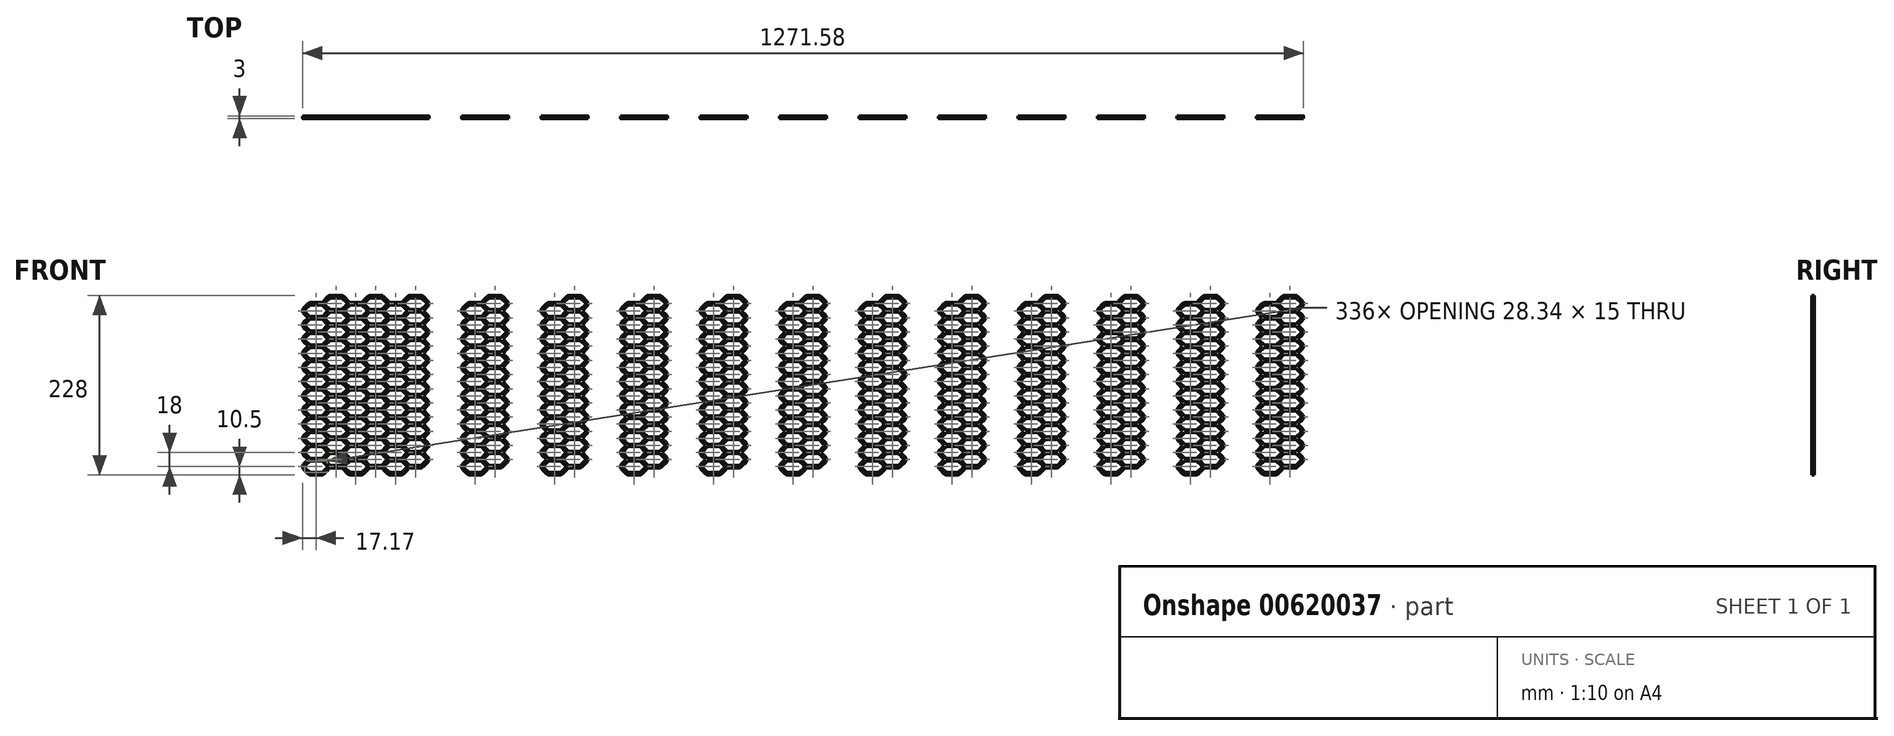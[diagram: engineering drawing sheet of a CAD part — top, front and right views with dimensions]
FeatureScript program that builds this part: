
annotation { "Feature Type Name" : "Feature", "Feature Type Description" : "" }
export const myFeature = defineFeature(function(context is Context, id is Id, definition is map)
    precondition{}
    {
        {
            var Q0;
            Q0=qCreatedBy(makeId("Front.planeOp"),FACE);
            var sketch = newSketch(context, id + "F0", { "sketchPlane" : qUnion([Q0])});
            skLineSegment(sketch, "E0.bottom", {"start": v(6.67, -7.5) * mm, "end": v(-6.67, -7.5) * mm});
            skLineSegment(sketch, "E0.top", {"start": v(6.67, 7.5) * mm, "end": v(-6.67, 7.5) * mm});
            skPoint(sketch, "E0.middle", {"position": v(0, 0) * mm});
            skLineSegment(sketch, "E1", {"start": v(-8.09, 6.91) * mm, "end": v(-13.59, 1.41) * mm});
            skLineSegment(sketch, "E2", {"start": v(-8.09, -6.91) * mm, "end": v(-13.59, -1.41) * mm});
            skLineSegment(sketch, "E3", {"start": v(8.09, 6.91) * mm, "end": v(13.59, 1.41) * mm});
            skLineSegment(sketch, "E4", {"start": v(13.59, -1.41) * mm, "end": v(8.09, -6.91) * mm});
            skPoint(sketch, "E5.visualSharp", {"position": v(-15, 0) * mm});
            skArc(sketch, "E5.filletArc", {"start": v(-13.59, 1.41) * mm, "mid": v(-14.17, 0) * mm, "end": v(-13.59, -1.41) * mm});
            skPoint(sketch, "E6.visualSharp", {"position": v(15, 0) * mm});
            skArc(sketch, "E6.filletArc", {"start": v(13.59, -1.41) * mm, "mid": v(14.17, 0) * mm, "end": v(13.59, 1.41) * mm});
            skPoint(sketch, "E7.visualSharp", {"position": v(7.5, -7.5) * mm});
            skArc(sketch, "E7.filletArc", {"start": v(6.67, -7.5) * mm, "mid": v(7.44, -7.35) * mm, "end": v(8.09, -6.91) * mm});
            skPoint(sketch, "E8.visualSharp", {"position": v(-7.5, -7.5) * mm});
            skArc(sketch, "E8.filletArc", {"start": v(-8.09, -6.91) * mm, "mid": v(-7.44, -7.35) * mm, "end": v(-6.67, -7.5) * mm});
            skArc(sketch, "E9.filletArc", {"start": v(-6.67, 7.5) * mm, "mid": v(-7.44, 7.35) * mm, "end": v(-8.09, 6.91) * mm});
            skArc(sketch, "E10.filletArc", {"start": v(8.09, 6.91) * mm, "mid": v(7.44, 7.35) * mm, "end": v(6.67, 7.5) * mm});
            skLineSegment(sketch, "E11.0.7.2", {"start": v(17.16, 160.1) * mm, "end": v(11.66, 154.6) * mm});
            skLineSegment(sketch, "E11.0.7.3", {"start": v(31.91, 160.68) * mm, "end": v(18.57, 160.68) * mm});
            skLineSegment(sketch, "E11.0.7.5", {"start": v(33.33, 160.1) * mm, "end": v(38.83, 154.6) * mm});
            skArc(sketch, "E11.0.7.7", {"start": v(33.33, 160.1) * mm, "mid": v(32.68, 160.53) * mm, "end": v(31.91, 160.68) * mm});
            skArc(sketch, "E11.0.7.10", {"start": v(18.57, 160.68) * mm, "mid": v(17.8, 160.53) * mm, "end": v(17.16, 160.1) * mm});
            skArc(sketch, "E12.0", {"start": v(10.2, 9.04) * mm, "mid": v(8.58, 10.12) * mm, "end": v(6.67, 10.5) * mm});
            skLineSegment(sketch, "E12.1", {"start": v(-10.2, -9.04) * mm, "end": v(-15.7, -3.54) * mm});
            skArc(sketch, "E12.2", {"start": v(-15.7, 3.54) * mm, "mid": v(-17.17, 0) * mm, "end": v(-15.7, -3.54) * mm});
            skLineSegment(sketch, "E12.3", {"start": v(-10.2, 9.04) * mm, "end": v(-15.7, 3.54) * mm});
            skArc(sketch, "E12.4", {"start": v(-6.67, 10.5) * mm, "mid": v(-8.58, 10.12) * mm, "end": v(-10.2, 9.04) * mm});
            skArc(sketch, "E12.5", {"start": v(-10.2, -9.04) * mm, "mid": v(-8.58, -10.12) * mm, "end": v(-6.67, -10.5) * mm});
            skLineSegment(sketch, "E12.6", {"start": v(6.67, 10.5) * mm, "end": v(-6.67, 10.5) * mm});
            skLineSegment(sketch, "E12.7", {"start": v(6.67, -10.5) * mm, "end": v(-6.67, -10.5) * mm});
            skArc(sketch, "E12.8", {"start": v(6.67, -10.5) * mm, "mid": v(8.58, -10.12) * mm, "end": v(10.2, -9.04) * mm});
            skLineSegment(sketch, "E12.9", {"start": v(15.7, -3.54) * mm, "end": v(10.2, -9.04) * mm});
            skArc(sketch, "E12.10", {"start": v(15.7, -3.54) * mm, "mid": v(17.17, 0) * mm, "end": v(15.7, 3.54) * mm});
            skLineSegment(sketch, "E12.11", {"start": v(10.2, 9.04) * mm, "end": v(15.7, 3.54) * mm});
            skLineSegment(sketch, "E13.bottom", {"start": v(-6.67, 5.5) * mm, "end": v(6.67, 5.5) * mm, "construction": true});
            skLineSegment(sketch, "E13.top", {"start": v(-6.67, -5.5) * mm, "end": v(6.67, -5.5) * mm, "construction": true});
            skLineSegment(sketch, "E13.left", {"start": v(-6.67, 5.5) * mm, "end": v(-6.67, -5.5) * mm, "construction": true});
            skLineSegment(sketch, "E13.right", {"start": v(6.67, 5.5) * mm, "end": v(6.67, -5.5) * mm, "construction": true});
            skSolve(sketch);
        }
        {
            var Q0;
            Q0=makeQuery(id+"F0.imprint","IMPRINT",FACE,{"disambiguationData":[TD([[makeQuery(id+"F0.imprint","IMPRINT",EDGE,{"derivedFrom":sQuery(id+"F0.wireOp",EDGE,"E0.bottom")}),1.0]])]});
            extrude(context, id + "F1", {"entities" : qUnion([Q0]), "depth" : 3 * mm, "offsetDistance" : 25 * mm});
        }
        {
            var Q0;
            Q0=qCreatedBy(makeId("Front.planeOp"),FACE);
            var sketch = newSketch(context, id + "F2", { "sketchPlane" : qUnion([Q0])});
            skLineSegment(sketch, "E14.0", {"start": v(6.67, -7.5) * mm, "end": v(-6.67, -7.5) * mm});
            skLineSegment(sketch, "E15.bottom", {"start": v(6.67, -25.5) * mm, "end": v(-6.67, -25.5) * mm});
            skLineSegment(sketch, "E15.top", {"start": v(6.67, -10.5) * mm, "end": v(-6.67, -10.5) * mm});
            skPoint(sketch, "E15.middle", {"position": v(0, -18) * mm});
            skLineSegment(sketch, "E16", {"start": v(-8.09, -11.09) * mm, "end": v(-13.59, -16.59) * mm});
            skLineSegment(sketch, "E17", {"start": v(-8.09, -24.91) * mm, "end": v(-13.59, -19.41) * mm});
            skLineSegment(sketch, "E18", {"start": v(8.09, -11.09) * mm, "end": v(13.59, -16.59) * mm});
            skLineSegment(sketch, "E19", {"start": v(13.59, -19.41) * mm, "end": v(8.09, -24.91) * mm});
            skPoint(sketch, "E20.visualSharp", {"position": v(-15, -18) * mm});
            skArc(sketch, "E20.filletArc", {"start": v(-13.59, -16.59) * mm, "mid": v(-14.17, -18) * mm, "end": v(-13.59, -19.41) * mm});
            skPoint(sketch, "E21.visualSharp", {"position": v(15, -18) * mm});
            skArc(sketch, "E21.filletArc", {"start": v(13.59, -19.41) * mm, "mid": v(14.17, -18) * mm, "end": v(13.59, -16.59) * mm});
            skPoint(sketch, "E22.visualSharp", {"position": v(7.5, -25.5) * mm});
            skArc(sketch, "E22.filletArc", {"start": v(6.67, -25.5) * mm, "mid": v(7.44, -25.35) * mm, "end": v(8.09, -24.91) * mm});
            skPoint(sketch, "E23.visualSharp", {"position": v(-7.5, -25.5) * mm});
            skArc(sketch, "E23.filletArc", {"start": v(-8.09, -24.91) * mm, "mid": v(-7.44, -25.35) * mm, "end": v(-6.67, -25.5) * mm});
            skArc(sketch, "E24.filletArc", {"start": v(-6.67, -10.5) * mm, "mid": v(-7.44, -10.65) * mm, "end": v(-8.09, -11.09) * mm});
            skArc(sketch, "E25.filletArc", {"start": v(8.09, -11.09) * mm, "mid": v(7.44, -10.65) * mm, "end": v(6.67, -10.5) * mm});
            skArc(sketch, "E26.0", {"start": v(10.2, -8.96) * mm, "mid": v(8.58, -7.88) * mm, "end": v(6.67, -7.5) * mm});
            skLineSegment(sketch, "E26.1", {"start": v(-10.2, -27.04) * mm, "end": v(-15.7, -21.54) * mm});
            skArc(sketch, "E26.2", {"start": v(-15.7, -14.46) * mm, "mid": v(-17.17, -18) * mm, "end": v(-15.7, -21.54) * mm});
            skLineSegment(sketch, "E26.3", {"start": v(-10.2, -8.96) * mm, "end": v(-15.7, -14.46) * mm});
            skArc(sketch, "E26.4", {"start": v(-6.67, -7.5) * mm, "mid": v(-8.58, -7.88) * mm, "end": v(-10.2, -8.96) * mm});
            skArc(sketch, "E26.5", {"start": v(-10.2, -27.04) * mm, "mid": v(-8.58, -28.12) * mm, "end": v(-6.67, -28.5) * mm});
            skLineSegment(sketch, "E26.7", {"start": v(6.67, -28.5) * mm, "end": v(-6.67, -28.5) * mm});
            skArc(sketch, "E26.8", {"start": v(6.67, -28.5) * mm, "mid": v(8.58, -28.12) * mm, "end": v(10.2, -27.04) * mm});
            skLineSegment(sketch, "E26.9", {"start": v(15.7, -21.54) * mm, "end": v(10.2, -27.04) * mm});
            skArc(sketch, "E26.10", {"start": v(15.7, -21.54) * mm, "mid": v(17.17, -18) * mm, "end": v(15.7, -14.46) * mm});
            skLineSegment(sketch, "E26.11", {"start": v(10.2, -8.96) * mm, "end": v(15.7, -14.46) * mm});
            skLineSegment(sketch, "E27.bottom", {"start": v(-6.67, -12.5) * mm, "end": v(6.67, -12.5) * mm, "construction": true});
            skLineSegment(sketch, "E27.top", {"start": v(-6.67, -23.5) * mm, "end": v(6.67, -23.5) * mm, "construction": true});
            skLineSegment(sketch, "E27.left", {"start": v(-6.67, -12.5) * mm, "end": v(-6.67, -23.5) * mm, "construction": true});
            skLineSegment(sketch, "E27.right", {"start": v(6.67, -12.5) * mm, "end": v(6.67, -23.5) * mm, "construction": true});
            skSolve(sketch);
        }
        {
            var Q0;
            Q0=makeQuery(id+"F2.imprint","IMPRINT",FACE,{"disambiguationData":[TD([[makeQuery(id+"F2.imprint","IMPRINT",EDGE,{"derivedFrom":sQuery(id+"F2.wireOp",EDGE,"E15.bottom")}),1.0]])]});
            extrude(context, id + "F3", {"entities" : qUnion([Q0]), "operationType" : NewBodyOperationType.ADD, "depth" : 3 * mm, "offsetDistance" : 25 * mm});
        }
        {
            var Q0;
            Q0=qCreatedBy(makeId("Front.planeOp"),FACE);
            var sketch = newSketch(context, id + "F4", { "sketchPlane" : qUnion([Q0])});
            skLineSegment(sketch, "E28.bottom", {"start": v(64.28, 40.04) * mm, "end": v(50.94, 40.04) * mm});
            skLineSegment(sketch, "E28.top", {"start": v(64.28, 55.04) * mm, "end": v(50.94, 55.04) * mm});
            skPoint(sketch, "E28.middle", {"position": v(57.61, 47.54) * mm});
            skLineSegment(sketch, "E29", {"start": v(49.53, 54.45) * mm, "end": v(44.03, 48.95) * mm});
            skLineSegment(sketch, "E30", {"start": v(49.53, 40.62) * mm, "end": v(44.03, 46.12) * mm});
            skLineSegment(sketch, "E31", {"start": v(65.7, 54.45) * mm, "end": v(71.2, 48.95) * mm});
            skLineSegment(sketch, "E32", {"start": v(71.2, 46.12) * mm, "end": v(65.7, 40.62) * mm});
            skPoint(sketch, "E33.visualSharp", {"position": v(42.61, 47.54) * mm});
            skArc(sketch, "E33.filletArc", {"start": v(44.03, 48.95) * mm, "mid": v(43.44, 47.54) * mm, "end": v(44.03, 46.12) * mm});
            skPoint(sketch, "E34.visualSharp", {"position": v(72.61, 47.54) * mm});
            skArc(sketch, "E34.filletArc", {"start": v(71.2, 46.12) * mm, "mid": v(71.78, 47.54) * mm, "end": v(71.2, 48.95) * mm});
            skPoint(sketch, "E35.visualSharp", {"position": v(65.11, 40.04) * mm});
            skArc(sketch, "E35.filletArc", {"start": v(64.28, 40.04) * mm, "mid": v(65.05, 40.2) * mm, "end": v(65.7, 40.62) * mm});
            skPoint(sketch, "E36.visualSharp", {"position": v(50.11, 40.04) * mm});
            skArc(sketch, "E36.filletArc", {"start": v(49.53, 40.62) * mm, "mid": v(50.18, 40.2) * mm, "end": v(50.94, 40.04) * mm});
            skArc(sketch, "E37.filletArc", {"start": v(50.94, 55.04) * mm, "mid": v(50.18, 54.89) * mm, "end": v(49.53, 54.45) * mm});
            skArc(sketch, "E38.filletArc", {"start": v(65.7, 54.45) * mm, "mid": v(65.05, 54.89) * mm, "end": v(64.28, 55.04) * mm});
            skArc(sketch, "E39.0", {"start": v(67.82, 56.57) * mm, "mid": v(66.2, 57.66) * mm, "end": v(64.28, 58.04) * mm});
            skLineSegment(sketch, "E39.1", {"start": v(47.4, 38.5) * mm, "end": v(41.9, 44) * mm});
            skArc(sketch, "E39.2", {"start": v(41.9, 51.07) * mm, "mid": v(40.44, 47.54) * mm, "end": v(41.9, 44) * mm});
            skLineSegment(sketch, "E39.3", {"start": v(47.4, 56.57) * mm, "end": v(41.9, 51.07) * mm});
            skArc(sketch, "E39.4", {"start": v(50.94, 58.04) * mm, "mid": v(49.03, 57.66) * mm, "end": v(47.4, 56.57) * mm});
            skArc(sketch, "E39.5", {"start": v(47.4, 38.5) * mm, "mid": v(49.03, 37.42) * mm, "end": v(50.94, 37.04) * mm});
            skLineSegment(sketch, "E39.6", {"start": v(64.28, 58.04) * mm, "end": v(50.94, 58.04) * mm});
            skLineSegment(sketch, "E39.7", {"start": v(64.28, 37.04) * mm, "end": v(50.94, 37.04) * mm});
            skArc(sketch, "E39.8", {"start": v(64.28, 37.04) * mm, "mid": v(66.2, 37.42) * mm, "end": v(67.82, 38.5) * mm});
            skLineSegment(sketch, "E39.9", {"start": v(73.32, 44) * mm, "end": v(67.82, 38.5) * mm});
            skArc(sketch, "E39.10", {"start": v(73.32, 44) * mm, "mid": v(74.78, 47.54) * mm, "end": v(73.32, 51.07) * mm});
            skLineSegment(sketch, "E39.11", {"start": v(67.82, 56.57) * mm, "end": v(73.32, 51.07) * mm});
            skLineSegment(sketch, "E40.bottom", {"start": v(50.94, 53.04) * mm, "end": v(64.28, 53.04) * mm, "construction": true});
            skLineSegment(sketch, "E40.top", {"start": v(50.94, 42.04) * mm, "end": v(64.28, 42.04) * mm, "construction": true});
            skLineSegment(sketch, "E40.left", {"start": v(50.94, 53.04) * mm, "end": v(50.94, 42.04) * mm, "construction": true});
            skLineSegment(sketch, "E40.right", {"start": v(64.28, 53.04) * mm, "end": v(64.28, 42.04) * mm, "construction": true});
            skLineSegment(sketch, "E41.0", {"start": v(15.7, -3.54) * mm, "end": v(10.24, -9) * mm});
            skLineSegment(sketch, "E42.bottom", {"start": v(31.91, -16.5) * mm, "end": v(18.57, -16.5) * mm});
            skLineSegment(sketch, "E42.top", {"start": v(31.91, -1.5) * mm, "end": v(18.57, -1.5) * mm});
            skPoint(sketch, "E42.middle", {"position": v(25.24, -9) * mm});
            skLineSegment(sketch, "E43", {"start": v(17.16, -2.09) * mm, "end": v(11.66, -7.59) * mm});
            skLineSegment(sketch, "E44", {"start": v(17.16, -15.91) * mm, "end": v(11.66, -10.41) * mm});
            skLineSegment(sketch, "E45", {"start": v(33.33, -2.09) * mm, "end": v(38.83, -7.59) * mm});
            skLineSegment(sketch, "E46", {"start": v(38.83, -10.41) * mm, "end": v(33.33, -15.91) * mm});
            skPoint(sketch, "E47.visualSharp", {"position": v(10.24, -9) * mm});
            skArc(sketch, "E47.filletArc", {"start": v(11.66, -7.59) * mm, "mid": v(11.07, -9) * mm, "end": v(11.66, -10.41) * mm});
            skPoint(sketch, "E48.visualSharp", {"position": v(40.24, -9) * mm});
            skArc(sketch, "E48.filletArc", {"start": v(38.83, -10.41) * mm, "mid": v(39.41, -9) * mm, "end": v(38.83, -7.59) * mm});
            skPoint(sketch, "E49.visualSharp", {"position": v(32.74, -16.5) * mm});
            skArc(sketch, "E49.filletArc", {"start": v(31.91, -16.5) * mm, "mid": v(32.68, -16.35) * mm, "end": v(33.33, -15.91) * mm});
            skPoint(sketch, "E50.visualSharp", {"position": v(17.74, -16.5) * mm});
            skArc(sketch, "E50.filletArc", {"start": v(17.16, -15.91) * mm, "mid": v(17.8, -16.35) * mm, "end": v(18.57, -16.5) * mm});
            skArc(sketch, "E51.filletArc", {"start": v(18.57, -1.5) * mm, "mid": v(17.8, -1.65) * mm, "end": v(17.16, -2.09) * mm});
            skArc(sketch, "E52.filletArc", {"start": v(33.33, -2.09) * mm, "mid": v(32.68, -1.65) * mm, "end": v(31.91, -1.5) * mm});
            skArc(sketch, "E53.0", {"start": v(35.45, 0.04) * mm, "mid": v(33.83, 1.12) * mm, "end": v(31.91, 1.5) * mm});
            skLineSegment(sketch, "E53.1", {"start": v(15.04, -18.04) * mm, "end": v(9.54, -12.54) * mm});
            skArc(sketch, "E53.2", {"start": v(9.54, -5.46) * mm, "mid": v(8.07, -9) * mm, "end": v(9.54, -12.54) * mm});
            skLineSegment(sketch, "E53.3", {"start": v(15.04, 0.04) * mm, "end": v(9.54, -5.46) * mm});
            skArc(sketch, "E53.4", {"start": v(18.57, 1.5) * mm, "mid": v(16.66, 1.12) * mm, "end": v(15.04, 0.04) * mm});
            skArc(sketch, "E53.5", {"start": v(15.04, -18.04) * mm, "mid": v(16.66, -19.12) * mm, "end": v(18.57, -19.5) * mm});
            skLineSegment(sketch, "E53.6", {"start": v(31.91, 1.5) * mm, "end": v(18.57, 1.5) * mm});
            skLineSegment(sketch, "E53.7", {"start": v(31.91, -19.5) * mm, "end": v(18.57, -19.5) * mm});
            skArc(sketch, "E53.8", {"start": v(31.91, -19.5) * mm, "mid": v(33.83, -19.12) * mm, "end": v(35.45, -18.04) * mm});
            skLineSegment(sketch, "E53.9", {"start": v(40.95, -12.54) * mm, "end": v(35.45, -18.04) * mm});
            skArc(sketch, "E53.10", {"start": v(40.95, -12.54) * mm, "mid": v(42.41, -9) * mm, "end": v(40.95, -5.46) * mm});
            skLineSegment(sketch, "E53.11", {"start": v(35.45, 0.04) * mm, "end": v(40.95, -5.46) * mm});
            skLineSegment(sketch, "E54.bottom", {"start": v(18.57, -3.5) * mm, "end": v(31.91, -3.5) * mm, "construction": true});
            skLineSegment(sketch, "E54.top", {"start": v(18.57, -14.5) * mm, "end": v(31.91, -14.5) * mm, "construction": true});
            skLineSegment(sketch, "E54.left", {"start": v(18.57, -3.5) * mm, "end": v(18.57, -14.5) * mm, "construction": true});
            skLineSegment(sketch, "E54.right", {"start": v(31.91, -3.5) * mm, "end": v(31.91, -14.5) * mm, "construction": true});
            skSolve(sketch);
        }
        {
            var Q0;
            Q0=makeQuery(id+"F4.imprint","IMPRINT",FACE,{"disambiguationData":[TD([[makeQuery(id+"F4.imprint","IMPRINT",EDGE,{"derivedFrom":sQuery(id+"F4.wireOp",EDGE,"E42.bottom")}),1.0]])]});
            extrude(context, id + "F5", {"entities" : qUnion([Q0]), "operationType" : NewBodyOperationType.ADD, "depth" : 3 * mm, "offsetDistance" : 25 * mm});
        }
        {
            var Q0;
            Q0=qCreatedBy(makeId("Front.planeOp"),FACE);
            var sketch = newSketch(context, id + "F6", { "sketchPlane" : qUnion([Q0])});
            skLineSegment(sketch, "E55.0", {"start": v(31.91, -1.5) * mm, "end": v(18.57, -1.5) * mm});
            skLineSegment(sketch, "E56.bottom", {"start": v(31.91, 1.5) * mm, "end": v(18.57, 1.5) * mm});
            skLineSegment(sketch, "E56.top", {"start": v(31.91, 16.5) * mm, "end": v(18.57, 16.5) * mm});
            skPoint(sketch, "E56.middle", {"position": v(25.24, 9) * mm});
            skLineSegment(sketch, "E57", {"start": v(17.16, 15.91) * mm, "end": v(11.66, 10.41) * mm});
            skLineSegment(sketch, "E58", {"start": v(17.16, 2.09) * mm, "end": v(11.66, 7.59) * mm});
            skLineSegment(sketch, "E59", {"start": v(33.33, 15.91) * mm, "end": v(38.83, 10.41) * mm});
            skLineSegment(sketch, "E60", {"start": v(38.83, 7.59) * mm, "end": v(33.33, 2.09) * mm});
            skPoint(sketch, "E61.visualSharp", {"position": v(10.24, 9) * mm});
            skArc(sketch, "E61.filletArc", {"start": v(11.66, 10.41) * mm, "mid": v(11.07, 9) * mm, "end": v(11.66, 7.59) * mm});
            skPoint(sketch, "E62.visualSharp", {"position": v(40.24, 9) * mm});
            skArc(sketch, "E62.filletArc", {"start": v(38.83, 7.59) * mm, "mid": v(39.41, 9) * mm, "end": v(38.83, 10.41) * mm});
            skPoint(sketch, "E63.visualSharp", {"position": v(32.74, 1.5) * mm});
            skArc(sketch, "E63.filletArc", {"start": v(31.91, 1.5) * mm, "mid": v(32.68, 1.65) * mm, "end": v(33.33, 2.09) * mm});
            skPoint(sketch, "E64.visualSharp", {"position": v(17.74, 1.5) * mm});
            skArc(sketch, "E64.filletArc", {"start": v(17.16, 2.09) * mm, "mid": v(17.8, 1.65) * mm, "end": v(18.57, 1.5) * mm});
            skArc(sketch, "E65.filletArc", {"start": v(18.57, 16.5) * mm, "mid": v(17.8, 16.35) * mm, "end": v(17.16, 15.91) * mm});
            skArc(sketch, "E66.filletArc", {"start": v(33.33, 15.91) * mm, "mid": v(32.68, 16.35) * mm, "end": v(31.91, 16.5) * mm});
            skArc(sketch, "E67.0", {"start": v(35.45, 18.04) * mm, "mid": v(33.83, 19.12) * mm, "end": v(31.91, 19.5) * mm});
            skLineSegment(sketch, "E67.1", {"start": v(15.04, -0.04) * mm, "end": v(9.54, 5.46) * mm});
            skArc(sketch, "E67.2", {"start": v(9.54, 12.54) * mm, "mid": v(8.07, 9) * mm, "end": v(9.54, 5.46) * mm});
            skLineSegment(sketch, "E67.3", {"start": v(15.04, 18.04) * mm, "end": v(9.54, 12.54) * mm});
            skArc(sketch, "E67.4", {"start": v(18.57, 19.5) * mm, "mid": v(16.66, 19.12) * mm, "end": v(15.04, 18.04) * mm});
            skArc(sketch, "E67.5", {"start": v(15.04, -0.04) * mm, "mid": v(16.66, -1.12) * mm, "end": v(18.57, -1.5) * mm});
            skLineSegment(sketch, "E67.6", {"start": v(31.91, 19.5) * mm, "end": v(18.57, 19.5) * mm});
            skArc(sketch, "E67.8", {"start": v(31.91, -1.5) * mm, "mid": v(33.83, -1.12) * mm, "end": v(35.45, -0.04) * mm});
            skLineSegment(sketch, "E67.9", {"start": v(40.95, 5.46) * mm, "end": v(35.45, -0.04) * mm});
            skArc(sketch, "E67.10", {"start": v(40.95, 5.46) * mm, "mid": v(42.41, 9) * mm, "end": v(40.95, 12.54) * mm});
            skLineSegment(sketch, "E67.11", {"start": v(35.45, 18.04) * mm, "end": v(40.95, 12.54) * mm});
            skLineSegment(sketch, "E68.bottom", {"start": v(18.57, 14.5) * mm, "end": v(31.91, 14.5) * mm, "construction": true});
            skLineSegment(sketch, "E68.top", {"start": v(18.57, 3.5) * mm, "end": v(31.91, 3.5) * mm, "construction": true});
            skLineSegment(sketch, "E68.left", {"start": v(18.57, 14.5) * mm, "end": v(18.57, 3.5) * mm, "construction": true});
            skLineSegment(sketch, "E68.right", {"start": v(31.91, 14.5) * mm, "end": v(31.91, 3.5) * mm, "construction": true});
            skSolve(sketch);
        }
        {
            var Q0;
            Q0=makeQuery(id+"F6.imprint","IMPRINT",FACE,{"disambiguationData":[TD([[makeQuery(id+"F6.imprint","IMPRINT",EDGE,{"derivedFrom":sQuery(id+"F6.wireOp",EDGE,"E56.bottom")}),1.0]])]});
            extrude(context, id + "F7", {"entities" : qUnion([Q0]), "operationType" : NewBodyOperationType.ADD, "depth" : 3 * mm, "offsetDistance" : 25 * mm});
        }
        {
            var Q0;
            Q0=makeQuery(id+"F1.opExtrude","SWEPT_BODY",BODY,{"disambiguationData":[OSD([sQuery(id+"F0.wireOp",EDGE,"E0.bottom"),sQuery(id+"F0.wireOp",EDGE,"E0.top"),sQuery(id+"F0.wireOp",EDGE,"E1"),sQuery(id+"F0.wireOp",EDGE,"E2"),sQuery(id+"F0.wireOp",EDGE,"E3"),sQuery(id+"F0.wireOp",EDGE,"E4"),sQuery(id+"F0.wireOp",EDGE,"E5.filletArc"),sQuery(id+"F0.wireOp",EDGE,"E6.filletArc"),sQuery(id+"F0.wireOp",EDGE,"E7.filletArc"),sQuery(id+"F0.wireOp",EDGE,"E8.filletArc"),sQuery(id+"F0.wireOp",EDGE,"E9.filletArc"),sQuery(id+"F0.wireOp",EDGE,"E10.filletArc"),sQuery(id+"F0.wireOp",EDGE,"E12.0"),sQuery(id+"F0.wireOp",EDGE,"E12.1"),sQuery(id+"F0.wireOp",EDGE,"E12.2"),sQuery(id+"F0.wireOp",EDGE,"E12.3"),sQuery(id+"F0.wireOp",EDGE,"E12.4"),sQuery(id+"F0.wireOp",EDGE,"E12.5"),sQuery(id+"F0.wireOp",EDGE,"E12.6"),sQuery(id+"F0.wireOp",EDGE,"E12.7"),sQuery(id+"F0.wireOp",EDGE,"E12.8"),sQuery(id+"F0.wireOp",EDGE,"E12.9"),sQuery(id+"F0.wireOp",EDGE,"E12.10"),sQuery(id+"F0.wireOp",EDGE,"E12.11")])]});
            transform(context, id + "F8", {"entities" : qUnion([Q0]), "transformType" : TransformType.TRANSLATION_3D, "dx" : 0 * mm, "dy" : 0 * mm, "dz" : 36 * mm, "makeCopy" : true});
        }
        {
            var Q0;
            Q0=makeQuery(id+"F8.opPattern","COPY",BODY,{"derivedFrom":makeQuery(id+"F1.opExtrude","SWEPT_BODY",BODY,{"disambiguationData":[OSD([sQuery(id+"F0.wireOp",EDGE,"E0.bottom"),sQuery(id+"F0.wireOp",EDGE,"E0.top"),sQuery(id+"F0.wireOp",EDGE,"E1"),sQuery(id+"F0.wireOp",EDGE,"E2"),sQuery(id+"F0.wireOp",EDGE,"E3"),sQuery(id+"F0.wireOp",EDGE,"E4"),sQuery(id+"F0.wireOp",EDGE,"E5.filletArc"),sQuery(id+"F0.wireOp",EDGE,"E6.filletArc"),sQuery(id+"F0.wireOp",EDGE,"E7.filletArc"),sQuery(id+"F0.wireOp",EDGE,"E8.filletArc"),sQuery(id+"F0.wireOp",EDGE,"E9.filletArc"),sQuery(id+"F0.wireOp",EDGE,"E10.filletArc"),sQuery(id+"F0.wireOp",EDGE,"E12.0"),sQuery(id+"F0.wireOp",EDGE,"E12.1"),sQuery(id+"F0.wireOp",EDGE,"E12.2"),sQuery(id+"F0.wireOp",EDGE,"E12.3"),sQuery(id+"F0.wireOp",EDGE,"E12.4"),sQuery(id+"F0.wireOp",EDGE,"E12.5"),sQuery(id+"F0.wireOp",EDGE,"E12.6"),sQuery(id+"F0.wireOp",EDGE,"E12.7"),sQuery(id+"F0.wireOp",EDGE,"E12.8"),sQuery(id+"F0.wireOp",EDGE,"E12.9"),sQuery(id+"F0.wireOp",EDGE,"E12.10"),sQuery(id+"F0.wireOp",EDGE,"E12.11")])]}),"instanceName":"1"});
            transform(context, id + "F9", {"entities" : qUnion([Q0]), "transformType" : TransformType.TRANSLATION_3D, "dx" : 0 * mm, "dy" : 0 * mm, "dz" : 36 * mm, "makeCopy" : true});
        }
        {
            var Q0;
            Q0=makeQuery(id+"F1.opExtrude","SWEPT_BODY",BODY,{"disambiguationData":[OSD([sQuery(id+"F0.wireOp",EDGE,"E0.bottom"),sQuery(id+"F0.wireOp",EDGE,"E0.top"),sQuery(id+"F0.wireOp",EDGE,"E1"),sQuery(id+"F0.wireOp",EDGE,"E2"),sQuery(id+"F0.wireOp",EDGE,"E3"),sQuery(id+"F0.wireOp",EDGE,"E4"),sQuery(id+"F0.wireOp",EDGE,"E5.filletArc"),sQuery(id+"F0.wireOp",EDGE,"E6.filletArc"),sQuery(id+"F0.wireOp",EDGE,"E7.filletArc"),sQuery(id+"F0.wireOp",EDGE,"E8.filletArc"),sQuery(id+"F0.wireOp",EDGE,"E9.filletArc"),sQuery(id+"F0.wireOp",EDGE,"E10.filletArc"),sQuery(id+"F0.wireOp",EDGE,"E12.0"),sQuery(id+"F0.wireOp",EDGE,"E12.1"),sQuery(id+"F0.wireOp",EDGE,"E12.2"),sQuery(id+"F0.wireOp",EDGE,"E12.3"),sQuery(id+"F0.wireOp",EDGE,"E12.4"),sQuery(id+"F0.wireOp",EDGE,"E12.5"),sQuery(id+"F0.wireOp",EDGE,"E12.6"),sQuery(id+"F0.wireOp",EDGE,"E12.7"),sQuery(id+"F0.wireOp",EDGE,"E12.8"),sQuery(id+"F0.wireOp",EDGE,"E12.9"),sQuery(id+"F0.wireOp",EDGE,"E12.10"),sQuery(id+"F0.wireOp",EDGE,"E12.11")])]});
            var Q1;
            Q1=makeQuery(id+"F8.opPattern","COPY",BODY,{"derivedFrom":makeQuery(id+"F1.opExtrude","SWEPT_BODY",BODY,{"disambiguationData":[OSD([sQuery(id+"F0.wireOp",EDGE,"E0.bottom"),sQuery(id+"F0.wireOp",EDGE,"E0.top"),sQuery(id+"F0.wireOp",EDGE,"E1"),sQuery(id+"F0.wireOp",EDGE,"E2"),sQuery(id+"F0.wireOp",EDGE,"E3"),sQuery(id+"F0.wireOp",EDGE,"E4"),sQuery(id+"F0.wireOp",EDGE,"E5.filletArc"),sQuery(id+"F0.wireOp",EDGE,"E6.filletArc"),sQuery(id+"F0.wireOp",EDGE,"E7.filletArc"),sQuery(id+"F0.wireOp",EDGE,"E8.filletArc"),sQuery(id+"F0.wireOp",EDGE,"E9.filletArc"),sQuery(id+"F0.wireOp",EDGE,"E10.filletArc"),sQuery(id+"F0.wireOp",EDGE,"E12.0"),sQuery(id+"F0.wireOp",EDGE,"E12.1"),sQuery(id+"F0.wireOp",EDGE,"E12.2"),sQuery(id+"F0.wireOp",EDGE,"E12.3"),sQuery(id+"F0.wireOp",EDGE,"E12.4"),sQuery(id+"F0.wireOp",EDGE,"E12.5"),sQuery(id+"F0.wireOp",EDGE,"E12.6"),sQuery(id+"F0.wireOp",EDGE,"E12.7"),sQuery(id+"F0.wireOp",EDGE,"E12.8"),sQuery(id+"F0.wireOp",EDGE,"E12.9"),sQuery(id+"F0.wireOp",EDGE,"E12.10"),sQuery(id+"F0.wireOp",EDGE,"E12.11")])]}),"instanceName":"1"});
            var Q2;
            Q2=makeQuery(id+"F9.opPattern","COPY",BODY,{"derivedFrom":makeQuery(id+"F8.opPattern","COPY",BODY,{"derivedFrom":makeQuery(id+"F1.opExtrude","SWEPT_BODY",BODY,{"disambiguationData":[OSD([sQuery(id+"F0.wireOp",EDGE,"E0.bottom"),sQuery(id+"F0.wireOp",EDGE,"E0.top"),sQuery(id+"F0.wireOp",EDGE,"E1"),sQuery(id+"F0.wireOp",EDGE,"E2"),sQuery(id+"F0.wireOp",EDGE,"E3"),sQuery(id+"F0.wireOp",EDGE,"E4"),sQuery(id+"F0.wireOp",EDGE,"E5.filletArc"),sQuery(id+"F0.wireOp",EDGE,"E6.filletArc"),sQuery(id+"F0.wireOp",EDGE,"E7.filletArc"),sQuery(id+"F0.wireOp",EDGE,"E8.filletArc"),sQuery(id+"F0.wireOp",EDGE,"E9.filletArc"),sQuery(id+"F0.wireOp",EDGE,"E10.filletArc"),sQuery(id+"F0.wireOp",EDGE,"E12.0"),sQuery(id+"F0.wireOp",EDGE,"E12.1"),sQuery(id+"F0.wireOp",EDGE,"E12.2"),sQuery(id+"F0.wireOp",EDGE,"E12.3"),sQuery(id+"F0.wireOp",EDGE,"E12.4"),sQuery(id+"F0.wireOp",EDGE,"E12.5"),sQuery(id+"F0.wireOp",EDGE,"E12.6"),sQuery(id+"F0.wireOp",EDGE,"E12.7"),sQuery(id+"F0.wireOp",EDGE,"E12.8"),sQuery(id+"F0.wireOp",EDGE,"E12.9"),sQuery(id+"F0.wireOp",EDGE,"E12.10"),sQuery(id+"F0.wireOp",EDGE,"E12.11")])]}),"instanceName":"1"}),"instanceName":"1"});
            booleanBodies(context, id + "F10", {"operationType" : BooleanOperationType.UNION, "tools" : qUnion([Q0, Q1, Q2])});
        }
        {
            var Q0;
            Q0=makeQuery(id+"F1.opExtrude","SWEPT_BODY",BODY,{"disambiguationData":[OSD([sQuery(id+"F0.wireOp",EDGE,"E0.bottom"),sQuery(id+"F0.wireOp",EDGE,"E0.top"),sQuery(id+"F0.wireOp",EDGE,"E1"),sQuery(id+"F0.wireOp",EDGE,"E2"),sQuery(id+"F0.wireOp",EDGE,"E3"),sQuery(id+"F0.wireOp",EDGE,"E4"),sQuery(id+"F0.wireOp",EDGE,"E5.filletArc"),sQuery(id+"F0.wireOp",EDGE,"E6.filletArc"),sQuery(id+"F0.wireOp",EDGE,"E7.filletArc"),sQuery(id+"F0.wireOp",EDGE,"E8.filletArc"),sQuery(id+"F0.wireOp",EDGE,"E9.filletArc"),sQuery(id+"F0.wireOp",EDGE,"E10.filletArc"),sQuery(id+"F0.wireOp",EDGE,"E12.0"),sQuery(id+"F0.wireOp",EDGE,"E12.1"),sQuery(id+"F0.wireOp",EDGE,"E12.2"),sQuery(id+"F0.wireOp",EDGE,"E12.3"),sQuery(id+"F0.wireOp",EDGE,"E12.4"),sQuery(id+"F0.wireOp",EDGE,"E12.5"),sQuery(id+"F0.wireOp",EDGE,"E12.6"),sQuery(id+"F0.wireOp",EDGE,"E12.7"),sQuery(id+"F0.wireOp",EDGE,"E12.8"),sQuery(id+"F0.wireOp",EDGE,"E12.9"),sQuery(id+"F0.wireOp",EDGE,"E12.10"),sQuery(id+"F0.wireOp",EDGE,"E12.11")])]});
            transform(context, id + "F11", {"entities" : qUnion([Q0]), "transformType" : TransformType.TRANSLATION_3D, "dx" : 0 * mm, "dy" : 0 * mm, "dz" : (36 * 3) * mm, "makeCopy" : true});
        }
        {
            var Q0;
            Q0=makeQuery(id+"F1.opExtrude","SWEPT_BODY",BODY,{"disambiguationData":[OSD([sQuery(id+"F0.wireOp",EDGE,"E0.bottom"),sQuery(id+"F0.wireOp",EDGE,"E0.top"),sQuery(id+"F0.wireOp",EDGE,"E1"),sQuery(id+"F0.wireOp",EDGE,"E2"),sQuery(id+"F0.wireOp",EDGE,"E3"),sQuery(id+"F0.wireOp",EDGE,"E4"),sQuery(id+"F0.wireOp",EDGE,"E5.filletArc"),sQuery(id+"F0.wireOp",EDGE,"E6.filletArc"),sQuery(id+"F0.wireOp",EDGE,"E7.filletArc"),sQuery(id+"F0.wireOp",EDGE,"E8.filletArc"),sQuery(id+"F0.wireOp",EDGE,"E9.filletArc"),sQuery(id+"F0.wireOp",EDGE,"E10.filletArc"),sQuery(id+"F0.wireOp",EDGE,"E12.0"),sQuery(id+"F0.wireOp",EDGE,"E12.1"),sQuery(id+"F0.wireOp",EDGE,"E12.2"),sQuery(id+"F0.wireOp",EDGE,"E12.3"),sQuery(id+"F0.wireOp",EDGE,"E12.4"),sQuery(id+"F0.wireOp",EDGE,"E12.5"),sQuery(id+"F0.wireOp",EDGE,"E12.6"),sQuery(id+"F0.wireOp",EDGE,"E12.7"),sQuery(id+"F0.wireOp",EDGE,"E12.8"),sQuery(id+"F0.wireOp",EDGE,"E12.9"),sQuery(id+"F0.wireOp",EDGE,"E12.10"),sQuery(id+"F0.wireOp",EDGE,"E12.11")])]});
            var Q1;
            Q1=makeQuery(id+"F11.opPattern","COPY",BODY,{"derivedFrom":makeQuery(id+"F1.opExtrude","SWEPT_BODY",BODY,{"disambiguationData":[OSD([sQuery(id+"F0.wireOp",EDGE,"E0.bottom"),sQuery(id+"F0.wireOp",EDGE,"E0.top"),sQuery(id+"F0.wireOp",EDGE,"E1"),sQuery(id+"F0.wireOp",EDGE,"E2"),sQuery(id+"F0.wireOp",EDGE,"E3"),sQuery(id+"F0.wireOp",EDGE,"E4"),sQuery(id+"F0.wireOp",EDGE,"E5.filletArc"),sQuery(id+"F0.wireOp",EDGE,"E6.filletArc"),sQuery(id+"F0.wireOp",EDGE,"E7.filletArc"),sQuery(id+"F0.wireOp",EDGE,"E8.filletArc"),sQuery(id+"F0.wireOp",EDGE,"E9.filletArc"),sQuery(id+"F0.wireOp",EDGE,"E10.filletArc"),sQuery(id+"F0.wireOp",EDGE,"E12.0"),sQuery(id+"F0.wireOp",EDGE,"E12.1"),sQuery(id+"F0.wireOp",EDGE,"E12.2"),sQuery(id+"F0.wireOp",EDGE,"E12.3"),sQuery(id+"F0.wireOp",EDGE,"E12.4"),sQuery(id+"F0.wireOp",EDGE,"E12.5"),sQuery(id+"F0.wireOp",EDGE,"E12.6"),sQuery(id+"F0.wireOp",EDGE,"E12.7"),sQuery(id+"F0.wireOp",EDGE,"E12.8"),sQuery(id+"F0.wireOp",EDGE,"E12.9"),sQuery(id+"F0.wireOp",EDGE,"E12.10"),sQuery(id+"F0.wireOp",EDGE,"E12.11")])]}),"instanceName":"1"});
            booleanBodies(context, id + "F12", {"operationType" : BooleanOperationType.UNION, "tools" : qUnion([Q0, Q1])});
        }
        {
            var Q0;
            Q0=makeQuery(id+"F1.opExtrude","SWEPT_BODY",BODY,{"disambiguationData":[OSD([sQuery(id+"F0.wireOp",EDGE,"E0.bottom"),sQuery(id+"F0.wireOp",EDGE,"E0.top"),sQuery(id+"F0.wireOp",EDGE,"E1"),sQuery(id+"F0.wireOp",EDGE,"E2"),sQuery(id+"F0.wireOp",EDGE,"E3"),sQuery(id+"F0.wireOp",EDGE,"E4"),sQuery(id+"F0.wireOp",EDGE,"E5.filletArc"),sQuery(id+"F0.wireOp",EDGE,"E6.filletArc"),sQuery(id+"F0.wireOp",EDGE,"E7.filletArc"),sQuery(id+"F0.wireOp",EDGE,"E8.filletArc"),sQuery(id+"F0.wireOp",EDGE,"E9.filletArc"),sQuery(id+"F0.wireOp",EDGE,"E10.filletArc"),sQuery(id+"F0.wireOp",EDGE,"E12.0"),sQuery(id+"F0.wireOp",EDGE,"E12.1"),sQuery(id+"F0.wireOp",EDGE,"E12.2"),sQuery(id+"F0.wireOp",EDGE,"E12.3"),sQuery(id+"F0.wireOp",EDGE,"E12.4"),sQuery(id+"F0.wireOp",EDGE,"E12.5"),sQuery(id+"F0.wireOp",EDGE,"E12.6"),sQuery(id+"F0.wireOp",EDGE,"E12.7"),sQuery(id+"F0.wireOp",EDGE,"E12.8"),sQuery(id+"F0.wireOp",EDGE,"E12.9"),sQuery(id+"F0.wireOp",EDGE,"E12.10"),sQuery(id+"F0.wireOp",EDGE,"E12.11")])]});
            transform(context, id + "F13", {"entities" : qUnion([Q0]), "transformType" : TransformType.TRANSLATION_3D, "dx" : 50.5 * mm, "dy" : 0 * mm, "dz" : 0 * mm, "makeCopy" : true});
        }
        {
            var Q0;
            Q0=makeQuery(id+"F1.opExtrude","SWEPT_BODY",BODY,{"disambiguationData":[OSD([sQuery(id+"F0.wireOp",EDGE,"E0.bottom"),sQuery(id+"F0.wireOp",EDGE,"E0.top"),sQuery(id+"F0.wireOp",EDGE,"E1"),sQuery(id+"F0.wireOp",EDGE,"E2"),sQuery(id+"F0.wireOp",EDGE,"E3"),sQuery(id+"F0.wireOp",EDGE,"E4"),sQuery(id+"F0.wireOp",EDGE,"E5.filletArc"),sQuery(id+"F0.wireOp",EDGE,"E6.filletArc"),sQuery(id+"F0.wireOp",EDGE,"E7.filletArc"),sQuery(id+"F0.wireOp",EDGE,"E8.filletArc"),sQuery(id+"F0.wireOp",EDGE,"E9.filletArc"),sQuery(id+"F0.wireOp",EDGE,"E10.filletArc"),sQuery(id+"F0.wireOp",EDGE,"E12.0"),sQuery(id+"F0.wireOp",EDGE,"E12.1"),sQuery(id+"F0.wireOp",EDGE,"E12.2"),sQuery(id+"F0.wireOp",EDGE,"E12.3"),sQuery(id+"F0.wireOp",EDGE,"E12.4"),sQuery(id+"F0.wireOp",EDGE,"E12.5"),sQuery(id+"F0.wireOp",EDGE,"E12.6"),sQuery(id+"F0.wireOp",EDGE,"E12.7"),sQuery(id+"F0.wireOp",EDGE,"E12.8"),sQuery(id+"F0.wireOp",EDGE,"E12.9"),sQuery(id+"F0.wireOp",EDGE,"E12.10"),sQuery(id+"F0.wireOp",EDGE,"E12.11")])]});
            transform(context, id + "F14", {"entities" : qUnion([Q0]), "transformType" : TransformType.TRANSLATION_3D, "dx" : 101 * mm, "dy" : 0 * mm, "dz" : 0 * mm, "makeCopy" : true});
        }
        {
            var Q0;
            Q0=makeQuery(id+"F14.opPattern","COPY",BODY,{"derivedFrom":makeQuery(id+"F1.opExtrude","SWEPT_BODY",BODY,{"disambiguationData":[OSD([sQuery(id+"F0.wireOp",EDGE,"E0.bottom"),sQuery(id+"F0.wireOp",EDGE,"E0.top"),sQuery(id+"F0.wireOp",EDGE,"E1"),sQuery(id+"F0.wireOp",EDGE,"E2"),sQuery(id+"F0.wireOp",EDGE,"E3"),sQuery(id+"F0.wireOp",EDGE,"E4"),sQuery(id+"F0.wireOp",EDGE,"E5.filletArc"),sQuery(id+"F0.wireOp",EDGE,"E6.filletArc"),sQuery(id+"F0.wireOp",EDGE,"E7.filletArc"),sQuery(id+"F0.wireOp",EDGE,"E8.filletArc"),sQuery(id+"F0.wireOp",EDGE,"E9.filletArc"),sQuery(id+"F0.wireOp",EDGE,"E10.filletArc"),sQuery(id+"F0.wireOp",EDGE,"E12.0"),sQuery(id+"F0.wireOp",EDGE,"E12.1"),sQuery(id+"F0.wireOp",EDGE,"E12.2"),sQuery(id+"F0.wireOp",EDGE,"E12.3"),sQuery(id+"F0.wireOp",EDGE,"E12.4"),sQuery(id+"F0.wireOp",EDGE,"E12.5"),sQuery(id+"F0.wireOp",EDGE,"E12.6"),sQuery(id+"F0.wireOp",EDGE,"E12.7"),sQuery(id+"F0.wireOp",EDGE,"E12.8"),sQuery(id+"F0.wireOp",EDGE,"E12.9"),sQuery(id+"F0.wireOp",EDGE,"E12.10"),sQuery(id+"F0.wireOp",EDGE,"E12.11")])]}),"instanceName":"1"});
            transform(context, id + "F15", {"entities" : qUnion([Q0]), "transformType" : TransformType.TRANSLATION_3D, "dx" : 101 * mm, "dy" : 0 * mm, "dz" : 0 * mm, "makeCopy" : true});
        }
        {
            var Q0;
            Q0=makeQuery(id+"F15.opPattern","COPY",BODY,{"derivedFrom":makeQuery(id+"F14.opPattern","COPY",BODY,{"derivedFrom":makeQuery(id+"F1.opExtrude","SWEPT_BODY",BODY,{"disambiguationData":[OSD([sQuery(id+"F0.wireOp",EDGE,"E0.bottom"),sQuery(id+"F0.wireOp",EDGE,"E0.top"),sQuery(id+"F0.wireOp",EDGE,"E1"),sQuery(id+"F0.wireOp",EDGE,"E2"),sQuery(id+"F0.wireOp",EDGE,"E3"),sQuery(id+"F0.wireOp",EDGE,"E4"),sQuery(id+"F0.wireOp",EDGE,"E5.filletArc"),sQuery(id+"F0.wireOp",EDGE,"E6.filletArc"),sQuery(id+"F0.wireOp",EDGE,"E7.filletArc"),sQuery(id+"F0.wireOp",EDGE,"E8.filletArc"),sQuery(id+"F0.wireOp",EDGE,"E9.filletArc"),sQuery(id+"F0.wireOp",EDGE,"E10.filletArc"),sQuery(id+"F0.wireOp",EDGE,"E12.0"),sQuery(id+"F0.wireOp",EDGE,"E12.1"),sQuery(id+"F0.wireOp",EDGE,"E12.2"),sQuery(id+"F0.wireOp",EDGE,"E12.3"),sQuery(id+"F0.wireOp",EDGE,"E12.4"),sQuery(id+"F0.wireOp",EDGE,"E12.5"),sQuery(id+"F0.wireOp",EDGE,"E12.6"),sQuery(id+"F0.wireOp",EDGE,"E12.7"),sQuery(id+"F0.wireOp",EDGE,"E12.8"),sQuery(id+"F0.wireOp",EDGE,"E12.9"),sQuery(id+"F0.wireOp",EDGE,"E12.10"),sQuery(id+"F0.wireOp",EDGE,"E12.11")])]}),"instanceName":"1"}),"instanceName":"1"});
            transform(context, id + "F16", {"entities" : qUnion([Q0]), "transformType" : TransformType.TRANSLATION_3D, "dx" : 101 * mm, "dy" : 0 * mm, "dz" : 0 * mm, "makeCopy" : true});
        }
        {
            var Q0;
            Q0=makeQuery(id+"F16.opPattern","COPY",BODY,{"derivedFrom":makeQuery(id+"F15.opPattern","COPY",BODY,{"derivedFrom":makeQuery(id+"F14.opPattern","COPY",BODY,{"derivedFrom":makeQuery(id+"F1.opExtrude","SWEPT_BODY",BODY,{"disambiguationData":[OSD([sQuery(id+"F0.wireOp",EDGE,"E0.bottom"),sQuery(id+"F0.wireOp",EDGE,"E0.top"),sQuery(id+"F0.wireOp",EDGE,"E1"),sQuery(id+"F0.wireOp",EDGE,"E2"),sQuery(id+"F0.wireOp",EDGE,"E3"),sQuery(id+"F0.wireOp",EDGE,"E4"),sQuery(id+"F0.wireOp",EDGE,"E5.filletArc"),sQuery(id+"F0.wireOp",EDGE,"E6.filletArc"),sQuery(id+"F0.wireOp",EDGE,"E7.filletArc"),sQuery(id+"F0.wireOp",EDGE,"E8.filletArc"),sQuery(id+"F0.wireOp",EDGE,"E9.filletArc"),sQuery(id+"F0.wireOp",EDGE,"E10.filletArc"),sQuery(id+"F0.wireOp",EDGE,"E12.0"),sQuery(id+"F0.wireOp",EDGE,"E12.1"),sQuery(id+"F0.wireOp",EDGE,"E12.2"),sQuery(id+"F0.wireOp",EDGE,"E12.3"),sQuery(id+"F0.wireOp",EDGE,"E12.4"),sQuery(id+"F0.wireOp",EDGE,"E12.5"),sQuery(id+"F0.wireOp",EDGE,"E12.6"),sQuery(id+"F0.wireOp",EDGE,"E12.7"),sQuery(id+"F0.wireOp",EDGE,"E12.8"),sQuery(id+"F0.wireOp",EDGE,"E12.9"),sQuery(id+"F0.wireOp",EDGE,"E12.10"),sQuery(id+"F0.wireOp",EDGE,"E12.11")])]}),"instanceName":"1"}),"instanceName":"1"}),"instanceName":"1"});
            transform(context, id + "F17", {"entities" : qUnion([Q0]), "transformType" : TransformType.TRANSLATION_3D, "dx" : 101 * mm, "dy" : 0 * mm, "dz" : 0 * mm, "makeCopy" : true});
        }
        {
            var Q0;
            Q0=makeQuery(id+"F17.opPattern","COPY",BODY,{"derivedFrom":makeQuery(id+"F16.opPattern","COPY",BODY,{"derivedFrom":makeQuery(id+"F15.opPattern","COPY",BODY,{"derivedFrom":makeQuery(id+"F14.opPattern","COPY",BODY,{"derivedFrom":makeQuery(id+"F1.opExtrude","SWEPT_BODY",BODY,{"disambiguationData":[OSD([sQuery(id+"F0.wireOp",EDGE,"E0.bottom"),sQuery(id+"F0.wireOp",EDGE,"E0.top"),sQuery(id+"F0.wireOp",EDGE,"E1"),sQuery(id+"F0.wireOp",EDGE,"E2"),sQuery(id+"F0.wireOp",EDGE,"E3"),sQuery(id+"F0.wireOp",EDGE,"E4"),sQuery(id+"F0.wireOp",EDGE,"E5.filletArc"),sQuery(id+"F0.wireOp",EDGE,"E6.filletArc"),sQuery(id+"F0.wireOp",EDGE,"E7.filletArc"),sQuery(id+"F0.wireOp",EDGE,"E8.filletArc"),sQuery(id+"F0.wireOp",EDGE,"E9.filletArc"),sQuery(id+"F0.wireOp",EDGE,"E10.filletArc"),sQuery(id+"F0.wireOp",EDGE,"E12.0"),sQuery(id+"F0.wireOp",EDGE,"E12.1"),sQuery(id+"F0.wireOp",EDGE,"E12.2"),sQuery(id+"F0.wireOp",EDGE,"E12.3"),sQuery(id+"F0.wireOp",EDGE,"E12.4"),sQuery(id+"F0.wireOp",EDGE,"E12.5"),sQuery(id+"F0.wireOp",EDGE,"E12.6"),sQuery(id+"F0.wireOp",EDGE,"E12.7"),sQuery(id+"F0.wireOp",EDGE,"E12.8"),sQuery(id+"F0.wireOp",EDGE,"E12.9"),sQuery(id+"F0.wireOp",EDGE,"E12.10"),sQuery(id+"F0.wireOp",EDGE,"E12.11")])]}),"instanceName":"1"}),"instanceName":"1"}),"instanceName":"1"}),"instanceName":"1"});
            transform(context, id + "F18", {"entities" : qUnion([Q0]), "transformType" : TransformType.TRANSLATION_3D, "dx" : 101 * mm, "dy" : 0 * mm, "dz" : 0 * mm, "makeCopy" : true});
        }
        {
            var Q0;
            Q0=makeQuery(id+"F18.opPattern","COPY",BODY,{"derivedFrom":makeQuery(id+"F17.opPattern","COPY",BODY,{"derivedFrom":makeQuery(id+"F16.opPattern","COPY",BODY,{"derivedFrom":makeQuery(id+"F15.opPattern","COPY",BODY,{"derivedFrom":makeQuery(id+"F14.opPattern","COPY",BODY,{"derivedFrom":makeQuery(id+"F1.opExtrude","SWEPT_BODY",BODY,{"disambiguationData":[OSD([sQuery(id+"F0.wireOp",EDGE,"E0.bottom"),sQuery(id+"F0.wireOp",EDGE,"E0.top"),sQuery(id+"F0.wireOp",EDGE,"E1"),sQuery(id+"F0.wireOp",EDGE,"E2"),sQuery(id+"F0.wireOp",EDGE,"E3"),sQuery(id+"F0.wireOp",EDGE,"E4"),sQuery(id+"F0.wireOp",EDGE,"E5.filletArc"),sQuery(id+"F0.wireOp",EDGE,"E6.filletArc"),sQuery(id+"F0.wireOp",EDGE,"E7.filletArc"),sQuery(id+"F0.wireOp",EDGE,"E8.filletArc"),sQuery(id+"F0.wireOp",EDGE,"E9.filletArc"),sQuery(id+"F0.wireOp",EDGE,"E10.filletArc"),sQuery(id+"F0.wireOp",EDGE,"E12.0"),sQuery(id+"F0.wireOp",EDGE,"E12.1"),sQuery(id+"F0.wireOp",EDGE,"E12.2"),sQuery(id+"F0.wireOp",EDGE,"E12.3"),sQuery(id+"F0.wireOp",EDGE,"E12.4"),sQuery(id+"F0.wireOp",EDGE,"E12.5"),sQuery(id+"F0.wireOp",EDGE,"E12.6"),sQuery(id+"F0.wireOp",EDGE,"E12.7"),sQuery(id+"F0.wireOp",EDGE,"E12.8"),sQuery(id+"F0.wireOp",EDGE,"E12.9"),sQuery(id+"F0.wireOp",EDGE,"E12.10"),sQuery(id+"F0.wireOp",EDGE,"E12.11")])]}),"instanceName":"1"}),"instanceName":"1"}),"instanceName":"1"}),"instanceName":"1"}),"instanceName":"1"});
            transform(context, id + "F19", {"entities" : qUnion([Q0]), "transformType" : TransformType.TRANSLATION_3D, "dx" : 101 * mm, "dy" : 0 * mm, "dz" : 0 * mm, "makeCopy" : true});
        }
        {
            var Q0;
            Q0=makeQuery(id+"F19.opPattern","COPY",BODY,{"derivedFrom":makeQuery(id+"F18.opPattern","COPY",BODY,{"derivedFrom":makeQuery(id+"F17.opPattern","COPY",BODY,{"derivedFrom":makeQuery(id+"F16.opPattern","COPY",BODY,{"derivedFrom":makeQuery(id+"F15.opPattern","COPY",BODY,{"derivedFrom":makeQuery(id+"F14.opPattern","COPY",BODY,{"derivedFrom":makeQuery(id+"F1.opExtrude","SWEPT_BODY",BODY,{"disambiguationData":[OSD([sQuery(id+"F0.wireOp",EDGE,"E0.bottom"),sQuery(id+"F0.wireOp",EDGE,"E0.top"),sQuery(id+"F0.wireOp",EDGE,"E1"),sQuery(id+"F0.wireOp",EDGE,"E2"),sQuery(id+"F0.wireOp",EDGE,"E3"),sQuery(id+"F0.wireOp",EDGE,"E4"),sQuery(id+"F0.wireOp",EDGE,"E5.filletArc"),sQuery(id+"F0.wireOp",EDGE,"E6.filletArc"),sQuery(id+"F0.wireOp",EDGE,"E7.filletArc"),sQuery(id+"F0.wireOp",EDGE,"E8.filletArc"),sQuery(id+"F0.wireOp",EDGE,"E9.filletArc"),sQuery(id+"F0.wireOp",EDGE,"E10.filletArc"),sQuery(id+"F0.wireOp",EDGE,"E12.0"),sQuery(id+"F0.wireOp",EDGE,"E12.1"),sQuery(id+"F0.wireOp",EDGE,"E12.2"),sQuery(id+"F0.wireOp",EDGE,"E12.3"),sQuery(id+"F0.wireOp",EDGE,"E12.4"),sQuery(id+"F0.wireOp",EDGE,"E12.5"),sQuery(id+"F0.wireOp",EDGE,"E12.6"),sQuery(id+"F0.wireOp",EDGE,"E12.7"),sQuery(id+"F0.wireOp",EDGE,"E12.8"),sQuery(id+"F0.wireOp",EDGE,"E12.9"),sQuery(id+"F0.wireOp",EDGE,"E12.10"),sQuery(id+"F0.wireOp",EDGE,"E12.11")])]}),"instanceName":"1"}),"instanceName":"1"}),"instanceName":"1"}),"instanceName":"1"}),"instanceName":"1"}),"instanceName":"1"});
            transform(context, id + "F20", {"entities" : qUnion([Q0]), "transformType" : TransformType.TRANSLATION_3D, "dx" : 101 * mm, "dy" : 0 * mm, "dz" : 0 * mm, "makeCopy" : true});
        }
        {
            var Q0;
            Q0=makeQuery(id+"F20.opPattern","COPY",BODY,{"derivedFrom":makeQuery(id+"F19.opPattern","COPY",BODY,{"derivedFrom":makeQuery(id+"F18.opPattern","COPY",BODY,{"derivedFrom":makeQuery(id+"F17.opPattern","COPY",BODY,{"derivedFrom":makeQuery(id+"F16.opPattern","COPY",BODY,{"derivedFrom":makeQuery(id+"F15.opPattern","COPY",BODY,{"derivedFrom":makeQuery(id+"F14.opPattern","COPY",BODY,{"derivedFrom":makeQuery(id+"F1.opExtrude","SWEPT_BODY",BODY,{"disambiguationData":[OSD([sQuery(id+"F0.wireOp",EDGE,"E0.bottom"),sQuery(id+"F0.wireOp",EDGE,"E0.top"),sQuery(id+"F0.wireOp",EDGE,"E1"),sQuery(id+"F0.wireOp",EDGE,"E2"),sQuery(id+"F0.wireOp",EDGE,"E3"),sQuery(id+"F0.wireOp",EDGE,"E4"),sQuery(id+"F0.wireOp",EDGE,"E5.filletArc"),sQuery(id+"F0.wireOp",EDGE,"E6.filletArc"),sQuery(id+"F0.wireOp",EDGE,"E7.filletArc"),sQuery(id+"F0.wireOp",EDGE,"E8.filletArc"),sQuery(id+"F0.wireOp",EDGE,"E9.filletArc"),sQuery(id+"F0.wireOp",EDGE,"E10.filletArc"),sQuery(id+"F0.wireOp",EDGE,"E12.0"),sQuery(id+"F0.wireOp",EDGE,"E12.1"),sQuery(id+"F0.wireOp",EDGE,"E12.2"),sQuery(id+"F0.wireOp",EDGE,"E12.3"),sQuery(id+"F0.wireOp",EDGE,"E12.4"),sQuery(id+"F0.wireOp",EDGE,"E12.5"),sQuery(id+"F0.wireOp",EDGE,"E12.6"),sQuery(id+"F0.wireOp",EDGE,"E12.7"),sQuery(id+"F0.wireOp",EDGE,"E12.8"),sQuery(id+"F0.wireOp",EDGE,"E12.9"),sQuery(id+"F0.wireOp",EDGE,"E12.10"),sQuery(id+"F0.wireOp",EDGE,"E12.11")])]}),"instanceName":"1"}),"instanceName":"1"}),"instanceName":"1"}),"instanceName":"1"}),"instanceName":"1"}),"instanceName":"1"}),"instanceName":"1"});
            transform(context, id + "F21", {"entities" : qUnion([Q0]), "transformType" : TransformType.TRANSLATION_3D, "dx" : 101 * mm, "dy" : 0 * mm, "dz" : 0 * mm, "makeCopy" : true});
        }
        {
            var Q0;
            Q0=makeQuery(id+"F21.opPattern","COPY",BODY,{"derivedFrom":makeQuery(id+"F20.opPattern","COPY",BODY,{"derivedFrom":makeQuery(id+"F19.opPattern","COPY",BODY,{"derivedFrom":makeQuery(id+"F18.opPattern","COPY",BODY,{"derivedFrom":makeQuery(id+"F17.opPattern","COPY",BODY,{"derivedFrom":makeQuery(id+"F16.opPattern","COPY",BODY,{"derivedFrom":makeQuery(id+"F15.opPattern","COPY",BODY,{"derivedFrom":makeQuery(id+"F14.opPattern","COPY",BODY,{"derivedFrom":makeQuery(id+"F1.opExtrude","SWEPT_BODY",BODY,{"disambiguationData":[OSD([sQuery(id+"F0.wireOp",EDGE,"E0.bottom"),sQuery(id+"F0.wireOp",EDGE,"E0.top"),sQuery(id+"F0.wireOp",EDGE,"E1"),sQuery(id+"F0.wireOp",EDGE,"E2"),sQuery(id+"F0.wireOp",EDGE,"E3"),sQuery(id+"F0.wireOp",EDGE,"E4"),sQuery(id+"F0.wireOp",EDGE,"E5.filletArc"),sQuery(id+"F0.wireOp",EDGE,"E6.filletArc"),sQuery(id+"F0.wireOp",EDGE,"E7.filletArc"),sQuery(id+"F0.wireOp",EDGE,"E8.filletArc"),sQuery(id+"F0.wireOp",EDGE,"E9.filletArc"),sQuery(id+"F0.wireOp",EDGE,"E10.filletArc"),sQuery(id+"F0.wireOp",EDGE,"E12.0"),sQuery(id+"F0.wireOp",EDGE,"E12.1"),sQuery(id+"F0.wireOp",EDGE,"E12.2"),sQuery(id+"F0.wireOp",EDGE,"E12.3"),sQuery(id+"F0.wireOp",EDGE,"E12.4"),sQuery(id+"F0.wireOp",EDGE,"E12.5"),sQuery(id+"F0.wireOp",EDGE,"E12.6"),sQuery(id+"F0.wireOp",EDGE,"E12.7"),sQuery(id+"F0.wireOp",EDGE,"E12.8"),sQuery(id+"F0.wireOp",EDGE,"E12.9"),sQuery(id+"F0.wireOp",EDGE,"E12.10"),sQuery(id+"F0.wireOp",EDGE,"E12.11")])]}),"instanceName":"1"}),"instanceName":"1"}),"instanceName":"1"}),"instanceName":"1"}),"instanceName":"1"}),"instanceName":"1"}),"instanceName":"1"}),"instanceName":"1"});
            transform(context, id + "F22", {"entities" : qUnion([Q0]), "transformType" : TransformType.TRANSLATION_3D, "dx" : 101 * mm, "dy" : 0 * mm, "dz" : 0 * mm, "makeCopy" : true});
        }
        {
            var Q0;
            Q0=makeQuery(id+"F22.opPattern","COPY",BODY,{"derivedFrom":makeQuery(id+"F21.opPattern","COPY",BODY,{"derivedFrom":makeQuery(id+"F20.opPattern","COPY",BODY,{"derivedFrom":makeQuery(id+"F19.opPattern","COPY",BODY,{"derivedFrom":makeQuery(id+"F18.opPattern","COPY",BODY,{"derivedFrom":makeQuery(id+"F17.opPattern","COPY",BODY,{"derivedFrom":makeQuery(id+"F16.opPattern","COPY",BODY,{"derivedFrom":makeQuery(id+"F15.opPattern","COPY",BODY,{"derivedFrom":makeQuery(id+"F14.opPattern","COPY",BODY,{"derivedFrom":makeQuery(id+"F1.opExtrude","SWEPT_BODY",BODY,{"disambiguationData":[OSD([sQuery(id+"F0.wireOp",EDGE,"E0.bottom"),sQuery(id+"F0.wireOp",EDGE,"E0.top"),sQuery(id+"F0.wireOp",EDGE,"E1"),sQuery(id+"F0.wireOp",EDGE,"E2"),sQuery(id+"F0.wireOp",EDGE,"E3"),sQuery(id+"F0.wireOp",EDGE,"E4"),sQuery(id+"F0.wireOp",EDGE,"E5.filletArc"),sQuery(id+"F0.wireOp",EDGE,"E6.filletArc"),sQuery(id+"F0.wireOp",EDGE,"E7.filletArc"),sQuery(id+"F0.wireOp",EDGE,"E8.filletArc"),sQuery(id+"F0.wireOp",EDGE,"E9.filletArc"),sQuery(id+"F0.wireOp",EDGE,"E10.filletArc"),sQuery(id+"F0.wireOp",EDGE,"E12.0"),sQuery(id+"F0.wireOp",EDGE,"E12.1"),sQuery(id+"F0.wireOp",EDGE,"E12.2"),sQuery(id+"F0.wireOp",EDGE,"E12.3"),sQuery(id+"F0.wireOp",EDGE,"E12.4"),sQuery(id+"F0.wireOp",EDGE,"E12.5"),sQuery(id+"F0.wireOp",EDGE,"E12.6"),sQuery(id+"F0.wireOp",EDGE,"E12.7"),sQuery(id+"F0.wireOp",EDGE,"E12.8"),sQuery(id+"F0.wireOp",EDGE,"E12.9"),sQuery(id+"F0.wireOp",EDGE,"E12.10"),sQuery(id+"F0.wireOp",EDGE,"E12.11")])]}),"instanceName":"1"}),"instanceName":"1"}),"instanceName":"1"}),"instanceName":"1"}),"instanceName":"1"}),"instanceName":"1"}),"instanceName":"1"}),"instanceName":"1"}),"instanceName":"1"});
            transform(context, id + "F23", {"entities" : qUnion([Q0]), "transformType" : TransformType.TRANSLATION_3D, "dx" : 101 * mm, "dy" : 0 * mm, "dz" : 0 * mm, "makeCopy" : true});
        }
        {
            var Q0;
            Q0=makeQuery(id+"F23.opPattern","COPY",BODY,{"derivedFrom":makeQuery(id+"F22.opPattern","COPY",BODY,{"derivedFrom":makeQuery(id+"F21.opPattern","COPY",BODY,{"derivedFrom":makeQuery(id+"F20.opPattern","COPY",BODY,{"derivedFrom":makeQuery(id+"F19.opPattern","COPY",BODY,{"derivedFrom":makeQuery(id+"F18.opPattern","COPY",BODY,{"derivedFrom":makeQuery(id+"F17.opPattern","COPY",BODY,{"derivedFrom":makeQuery(id+"F16.opPattern","COPY",BODY,{"derivedFrom":makeQuery(id+"F15.opPattern","COPY",BODY,{"derivedFrom":makeQuery(id+"F14.opPattern","COPY",BODY,{"derivedFrom":makeQuery(id+"F1.opExtrude","SWEPT_BODY",BODY,{"disambiguationData":[OSD([sQuery(id+"F0.wireOp",EDGE,"E0.bottom"),sQuery(id+"F0.wireOp",EDGE,"E0.top"),sQuery(id+"F0.wireOp",EDGE,"E1"),sQuery(id+"F0.wireOp",EDGE,"E2"),sQuery(id+"F0.wireOp",EDGE,"E3"),sQuery(id+"F0.wireOp",EDGE,"E4"),sQuery(id+"F0.wireOp",EDGE,"E5.filletArc"),sQuery(id+"F0.wireOp",EDGE,"E6.filletArc"),sQuery(id+"F0.wireOp",EDGE,"E7.filletArc"),sQuery(id+"F0.wireOp",EDGE,"E8.filletArc"),sQuery(id+"F0.wireOp",EDGE,"E9.filletArc"),sQuery(id+"F0.wireOp",EDGE,"E10.filletArc"),sQuery(id+"F0.wireOp",EDGE,"E12.0"),sQuery(id+"F0.wireOp",EDGE,"E12.1"),sQuery(id+"F0.wireOp",EDGE,"E12.2"),sQuery(id+"F0.wireOp",EDGE,"E12.3"),sQuery(id+"F0.wireOp",EDGE,"E12.4"),sQuery(id+"F0.wireOp",EDGE,"E12.5"),sQuery(id+"F0.wireOp",EDGE,"E12.6"),sQuery(id+"F0.wireOp",EDGE,"E12.7"),sQuery(id+"F0.wireOp",EDGE,"E12.8"),sQuery(id+"F0.wireOp",EDGE,"E12.9"),sQuery(id+"F0.wireOp",EDGE,"E12.10"),sQuery(id+"F0.wireOp",EDGE,"E12.11")])]}),"instanceName":"1"}),"instanceName":"1"}),"instanceName":"1"}),"instanceName":"1"}),"instanceName":"1"}),"instanceName":"1"}),"instanceName":"1"}),"instanceName":"1"}),"instanceName":"1"}),"instanceName":"1"});
            transform(context, id + "F24", {"entities" : qUnion([Q0]), "transformType" : TransformType.TRANSLATION_3D, "dx" : 101 * mm, "dy" : 0 * mm, "dz" : 0 * mm, "makeCopy" : true});
        }
        {
            var Q0;
            Q0=makeQuery(id+"F24.opPattern","COPY",BODY,{"derivedFrom":makeQuery(id+"F23.opPattern","COPY",BODY,{"derivedFrom":makeQuery(id+"F22.opPattern","COPY",BODY,{"derivedFrom":makeQuery(id+"F21.opPattern","COPY",BODY,{"derivedFrom":makeQuery(id+"F20.opPattern","COPY",BODY,{"derivedFrom":makeQuery(id+"F19.opPattern","COPY",BODY,{"derivedFrom":makeQuery(id+"F18.opPattern","COPY",BODY,{"derivedFrom":makeQuery(id+"F17.opPattern","COPY",BODY,{"derivedFrom":makeQuery(id+"F16.opPattern","COPY",BODY,{"derivedFrom":makeQuery(id+"F15.opPattern","COPY",BODY,{"derivedFrom":makeQuery(id+"F14.opPattern","COPY",BODY,{"derivedFrom":makeQuery(id+"F1.opExtrude","SWEPT_BODY",BODY,{"disambiguationData":[OSD([sQuery(id+"F0.wireOp",EDGE,"E0.bottom"),sQuery(id+"F0.wireOp",EDGE,"E0.top"),sQuery(id+"F0.wireOp",EDGE,"E1"),sQuery(id+"F0.wireOp",EDGE,"E2"),sQuery(id+"F0.wireOp",EDGE,"E3"),sQuery(id+"F0.wireOp",EDGE,"E4"),sQuery(id+"F0.wireOp",EDGE,"E5.filletArc"),sQuery(id+"F0.wireOp",EDGE,"E6.filletArc"),sQuery(id+"F0.wireOp",EDGE,"E7.filletArc"),sQuery(id+"F0.wireOp",EDGE,"E8.filletArc"),sQuery(id+"F0.wireOp",EDGE,"E9.filletArc"),sQuery(id+"F0.wireOp",EDGE,"E10.filletArc"),sQuery(id+"F0.wireOp",EDGE,"E12.0"),sQuery(id+"F0.wireOp",EDGE,"E12.1"),sQuery(id+"F0.wireOp",EDGE,"E12.2"),sQuery(id+"F0.wireOp",EDGE,"E12.3"),sQuery(id+"F0.wireOp",EDGE,"E12.4"),sQuery(id+"F0.wireOp",EDGE,"E12.5"),sQuery(id+"F0.wireOp",EDGE,"E12.6"),sQuery(id+"F0.wireOp",EDGE,"E12.7"),sQuery(id+"F0.wireOp",EDGE,"E12.8"),sQuery(id+"F0.wireOp",EDGE,"E12.9"),sQuery(id+"F0.wireOp",EDGE,"E12.10"),sQuery(id+"F0.wireOp",EDGE,"E12.11")])]}),"instanceName":"1"}),"instanceName":"1"}),"instanceName":"1"}),"instanceName":"1"}),"instanceName":"1"}),"instanceName":"1"}),"instanceName":"1"}),"instanceName":"1"}),"instanceName":"1"}),"instanceName":"1"}),"instanceName":"1"});
            transform(context, id + "F25", {"entities" : qUnion([Q0]), "transformType" : TransformType.TRANSLATION_3D, "dx" : 101 * mm, "dy" : 0 * mm, "dz" : 0 * mm, "makeCopy" : true});
        }
    });
